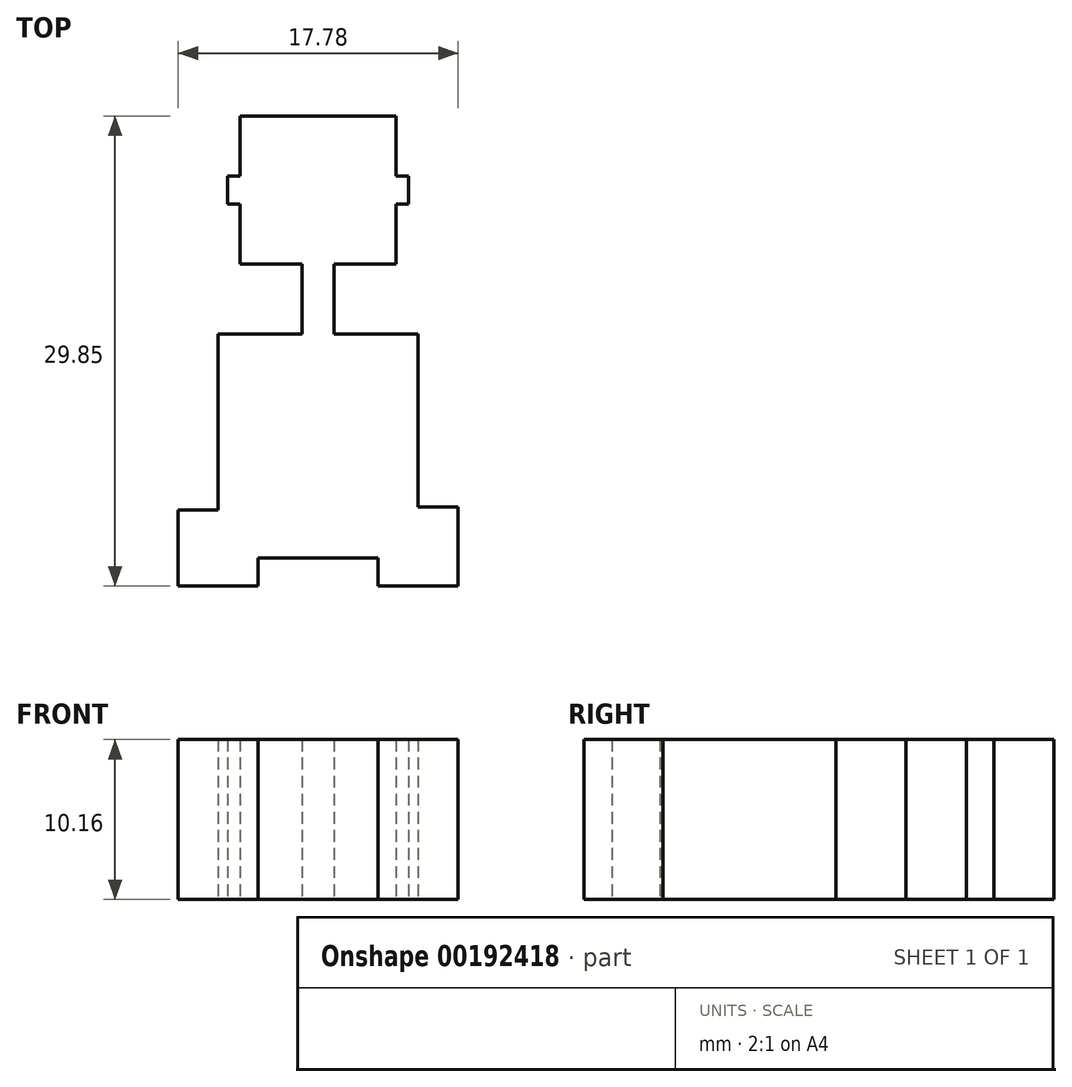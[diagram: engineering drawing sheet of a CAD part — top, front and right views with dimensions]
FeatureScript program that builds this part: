
annotation { "Feature Type Name" : "Feature", "Feature Type Description" : "" }
export const myFeature = defineFeature(function(context is Context, id is Id, definition is map)
    precondition{}
    {
        {
            var Q0;
            Q0=qCreatedBy(makeId("Top.planeOp"),FACE);
            var sketch = newSketch(context, id + "F0", { "sketchPlane" : qUnion([Q0])});
            skLineSegment(sketch, "E0.bottom", {"start": v(-22.02, -7.97) * mm, "end": v(-29.64, -7.97) * mm});
            skLineSegment(sketch, "E0.top", {"start": v(-19.48, 6.26) * mm, "end": v(-24.81, 6.26) * mm});
            skLineSegment(sketch, "E0.left", {"start": v(-19.48, -4.73) * mm, "end": v(-19.48, 6.26) * mm});
            skLineSegment(sketch, "E0.right", {"start": v(-32.18, -4.92) * mm, "end": v(-32.18, 6.26) * mm});
            skPoint(sketch, "E0.middle", {"position": v(-25.83, -0.86) * mm});
            skLineSegment(sketch, "E1.left", {"start": v(-24.81, 10.7) * mm, "end": v(-24.81, 6.26) * mm});
            skLineSegment(sketch, "E1.right", {"start": v(-26.85, 10.7) * mm, "end": v(-26.85, 6.26) * mm});
            skPoint(sketch, "E1.middle", {"position": v(-25.83, 6.26) * mm});
            skLineSegment(sketch, "E2.bottom", {"start": v(-30.78, 10.7) * mm, "end": v(-26.85, 10.7) * mm});
            skLineSegment(sketch, "E2.top", {"start": v(-30.78, 20.1) * mm, "end": v(-20.88, 20.1) * mm});
            skLineSegment(sketch, "E2.left", {"start": v(-30.78, 10.7) * mm, "end": v(-30.78, 14.52) * mm});
            skLineSegment(sketch, "E2.right", {"start": v(-20.88, 10.7) * mm, "end": v(-20.88, 14.52) * mm});
            skPoint(sketch, "E2.middle", {"position": v(-25.83, 15.4) * mm});
            skPoint(sketch, "E2.middle.positionSnap0", {"position": v(-25.83, 10.7) * mm});
            skPoint(sketch, "E2.cornerSnap0", {"position": v(-25.83, 10.7) * mm});
            skPoint(sketch, "E2.centerSnap0", {"position": v(-25.83, 10.7) * mm});
            skLineSegment(sketch, "E3.bottom", {"start": v(-34.72, -9.75) * mm, "end": v(-29.64, -9.75) * mm});
            skLineSegment(sketch, "E3.top", {"start": v(-34.72, -4.92) * mm, "end": v(-32.18, -4.92) * mm});
            skLineSegment(sketch, "E3.left", {"start": v(-34.72, -9.75) * mm, "end": v(-34.72, -4.92) * mm});
            skLineSegment(sketch, "E3.right", {"start": v(-29.64, -9.75) * mm, "end": v(-29.64, -7.97) * mm});
            skPoint(sketch, "E3.middle", {"position": v(-32.18, -7.33) * mm});
            skLineSegment(sketch, "E4.bottom", {"start": v(-22.02, -9.75) * mm, "end": v(-16.94, -9.75) * mm});
            skLineSegment(sketch, "E4.top", {"start": v(-19.48, -4.73) * mm, "end": v(-16.94, -4.73) * mm});
            skLineSegment(sketch, "E4.left", {"start": v(-22.02, -9.75) * mm, "end": v(-22.02, -7.97) * mm});
            skLineSegment(sketch, "E4.right", {"start": v(-16.94, -9.75) * mm, "end": v(-16.94, -4.73) * mm});
            skPoint(sketch, "E5.orphan", {"position": v(-24.81, 1.81) * mm});
            skPoint(sketch, "E6.orphan", {"position": v(-26.85, 1.81) * mm});
            skLineSegment(sketch, "E7.trimOffspring", {"start": v(-26.85, 6.26) * mm, "end": v(-32.18, 6.26) * mm});
            skLineSegment(sketch, "E8.trimOffspring", {"start": v(-24.81, 10.7) * mm, "end": v(-20.88, 10.7) * mm});
            skPoint(sketch, "E9.orphan", {"position": v(-29.64, -4.92) * mm});
            skPoint(sketch, "E10.orphan", {"position": v(-32.18, -7.97) * mm});
            skPoint(sketch, "E11.orphan", {"position": v(-19.48, -7.97) * mm});
            skLineSegment(sketch, "E12.bottom", {"start": v(-31.6, 16.28) * mm, "end": v(-30.78, 16.28) * mm});
            skLineSegment(sketch, "E12.top", {"start": v(-31.6, 14.52) * mm, "end": v(-30.78, 14.52) * mm});
            skLineSegment(sketch, "E12.left", {"start": v(-31.6, 16.28) * mm, "end": v(-31.6, 14.52) * mm});
            skPoint(sketch, "E12.middle", {"position": v(-30.78, 15.4) * mm});
            skLineSegment(sketch, "E13.bottom", {"start": v(-20.88, 16.28) * mm, "end": v(-20.08, 16.28) * mm});
            skLineSegment(sketch, "E13.top", {"start": v(-20.88, 14.52) * mm, "end": v(-20.08, 14.52) * mm});
            skLineSegment(sketch, "E13.right", {"start": v(-20.08, 16.28) * mm, "end": v(-20.08, 14.52) * mm});
            skPoint(sketch, "E13.middle", {"position": v(-20.88, 15.4) * mm});
            skPoint(sketch, "E13.left.start.orphan", {"position": v(-21.68, 16.28) * mm});
            skPoint(sketch, "E14.orphan", {"position": v(-21.68, 14.52) * mm});
            skLineSegment(sketch, "E15.trimOffspring", {"start": v(-20.88, 16.28) * mm, "end": v(-20.88, 20.1) * mm});
            skPoint(sketch, "E16.orphan", {"position": v(-29.97, 16.28) * mm});
            skLineSegment(sketch, "E17.trimOffspring", {"start": v(-30.78, 16.28) * mm, "end": v(-30.78, 20.1) * mm});
            skPoint(sketch, "E18.orphan", {"position": v(-29.97, 14.52) * mm});
            skSolve(sketch);
        }
        {
            var Q0;
            Q0 = qSketchRegion(id + "F0", true);
            extrude(context, id + "F1", {"entities" : qUnion([Q0]), "endBound" : BoundingType.SYMMETRIC, "depth" : 10.16 * mm});
        }
    });
